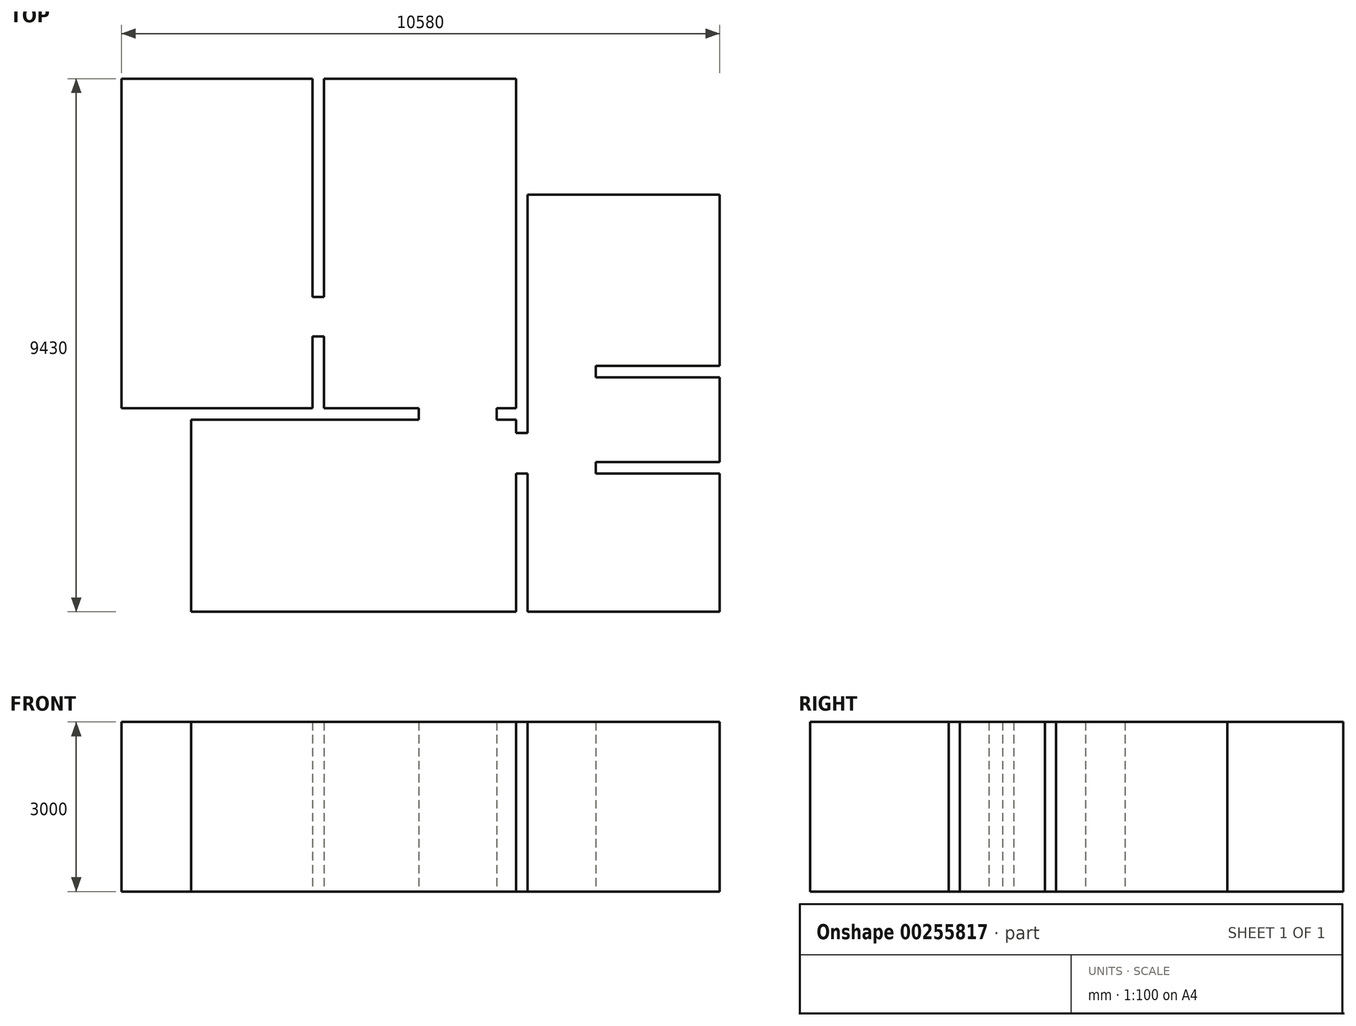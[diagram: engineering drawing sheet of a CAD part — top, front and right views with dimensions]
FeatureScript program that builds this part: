
annotation { "Feature Type Name" : "Feature", "Feature Type Description" : "" }
export const myFeature = defineFeature(function(context is Context, id is Id, definition is map)
    precondition{}
    {
        {
            var Q0;
            Q0=qCreatedBy(makeId("Top.planeOp"),FACE);
            var sketch = newSketch(context, id + "F0", { "sketchPlane" : qUnion([Q0])});
            skLineSegment(sketch, "E0", {"start": v(0, 0) * mm, "end": v(0, 5830) * mm});
            skLineSegment(sketch, "E1", {"start": v(0, 5830) * mm, "end": v(3380, 5830) * mm});
            skLineSegment(sketch, "E2", {"start": v(3380, 5830) * mm, "end": v(3380, 1970) * mm});
            skLineSegment(sketch, "E3", {"start": v(3380, 1970) * mm, "end": v(3580, 1970) * mm});
            skLineSegment(sketch, "E4", {"start": v(3580, 1970) * mm, "end": v(3580, 5830) * mm});
            skLineSegment(sketch, "E5", {"start": v(3580, 5830) * mm, "end": v(6980, 5830) * mm});
            skLineSegment(sketch, "E6", {"start": v(6980, 5830) * mm, "end": v(6980, 0) * mm});
            skLineSegment(sketch, "E7", {"start": v(6980, -1151.93) * mm, "end": v(6980, -3600) * mm});
            skLineSegment(sketch, "E8", {"start": v(6980, -3600) * mm, "end": v(1230, -3600) * mm});
            skLineSegment(sketch, "E9", {"start": v(1230, -3600) * mm, "end": v(1230, -200) * mm});
            skLineSegment(sketch, "E10", {"start": v(0, 0) * mm, "end": v(1230, 0) * mm});
            skLineSegment(sketch, "E11", {"start": v(1230, 0) * mm, "end": v(3380, 0) * mm});
            skLineSegment(sketch, "E12", {"start": v(3580, 1270) * mm, "end": v(3580, 0) * mm});
            skLineSegment(sketch, "E13", {"start": v(3580, 1270) * mm, "end": v(3380, 1270) * mm});
            skLineSegment(sketch, "E14", {"start": v(3380, 1270) * mm, "end": v(3380, 0) * mm});
            skLineSegment(sketch, "E15", {"start": v(6980, -1151.93) * mm, "end": v(7180, -1151.93) * mm});
            skLineSegment(sketch, "E16", {"start": v(7180, -1151.93) * mm, "end": v(7180, -3600) * mm});
            skLineSegment(sketch, "E17", {"start": v(7180, -3600) * mm, "end": v(10580, -3600) * mm});
            skLineSegment(sketch, "E18", {"start": v(1230, -200) * mm, "end": v(5260, -200) * mm});
            skLineSegment(sketch, "E19", {"start": v(5260, -200) * mm, "end": v(5260, 0) * mm});
            skLineSegment(sketch, "E20.trimOffspring", {"start": v(3580, 0) * mm, "end": v(5260, 0) * mm});
            skLineSegment(sketch, "E21", {"start": v(10580, -2375.97) * mm, "end": v(10580, -1151.93) * mm});
            skLineSegment(sketch, "E22", {"start": v(10580, 750) * mm, "end": v(10580, 3780) * mm});
            skLineSegment(sketch, "E23", {"start": v(10580, 3780) * mm, "end": v(7180, 3780) * mm});
            skPoint(sketch, "E23.endSnap0", {"position": v(6980, 2915) * mm});
            skLineSegment(sketch, "E24", {"start": v(7180, 3780) * mm, "end": v(7180, 0) * mm});
            skPoint(sketch, "E25.orphan", {"position": v(6980, 3780) * mm});
            skLineSegment(sketch, "E26", {"start": v(10580, -1151.93) * mm, "end": v(8390, -1151.93) * mm});
            skLineSegment(sketch, "E27", {"start": v(8390, -1151.93) * mm, "end": v(8390, -951.93) * mm});
            skLineSegment(sketch, "E28", {"start": v(8390, -951.93) * mm, "end": v(10580, -951.93) * mm});
            skLineSegment(sketch, "E29.trimOffspring", {"start": v(10580, -951.93) * mm, "end": v(10580, 550) * mm});
            skPoint(sketch, "E30.start.orphan", {"position": v(10580, -2375.97) * mm});
            skLineSegment(sketch, "E31", {"start": v(10580, -3600) * mm, "end": v(10580, -3075.97) * mm});
            skLineSegment(sketch, "E32", {"start": v(7180, -200) * mm, "end": v(7180, 0) * mm});
            skLineSegment(sketch, "E33", {"start": v(6980, 0) * mm, "end": v(6635.32, 0) * mm});
            skLineSegment(sketch, "E34", {"start": v(6635.32, 0) * mm, "end": v(6635.32, -200) * mm});
            skLineSegment(sketch, "E35", {"start": v(6980, -200) * mm, "end": v(6635.32, -200) * mm});
            skLineSegment(sketch, "E36", {"start": v(6980, -200) * mm, "end": v(6980, -438.14) * mm});
            skLineSegment(sketch, "E37", {"start": v(6980, -438.14) * mm, "end": v(7181.24, -438.14) * mm});
            skLineSegment(sketch, "E38", {"start": v(7181.24, -438.14) * mm, "end": v(7180, -200) * mm});
            skLineSegment(sketch, "E39", {"start": v(10580, -3075.97) * mm, "end": v(10580, -2375.97) * mm});
            skLineSegment(sketch, "E40", {"start": v(10580, 550) * mm, "end": v(8390, 550) * mm});
            skLineSegment(sketch, "E41", {"start": v(8390, 550) * mm, "end": v(8390, 750) * mm});
            skLineSegment(sketch, "E42", {"start": v(8390, 750) * mm, "end": v(10580, 750) * mm});
            skSolve(sketch);
        }
        {
            var Q0;
            Q0=makeQuery(id+"F0.imprint","IMPRINT",FACE,{"disambiguationData":[TD([[makeQuery(id+"F0.imprint","IMPRINT",EDGE,{"derivedFrom":sQuery(id+"F0.wireOp",EDGE,"E0")}),-1.0]])]});
            extrude(context, id + "F1", {"entities" : qUnion([Q0]), "depth" : 3000 * mm, "offsetDistance" : 25 * mm});
        }
    });
